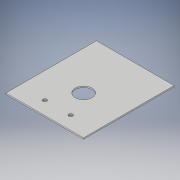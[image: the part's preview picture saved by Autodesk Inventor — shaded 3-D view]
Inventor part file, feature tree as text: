
AUTODESK INVENTOR PART (.ipt)
format: ipt  version: 2019 (Build 230136000, 136)  size: 104,960 bytes
history: native  units: mm
features: extrude x3, sketch x3
ambient origin geometry x8: Origin, YZ Plane, XZ Plane, XY Plane, X Axis, Y Axis, Z Axis, Center Point
bodies: Solid1 (feature_tree)
feature tree (6):
  extrude  "Extrusion1"  Depth=70.0mm
  extrude  "Extrusion2"  Depth=1.0mm
  extrude  "Extrusion3"  Depth=1.0mm TaperAngle=0.0deg
  sketch  "Sketch1"  dims[d0=60.0mm d1=70.0mm]
  sketch  "Sketch2"  dims[d2=1.0mm d3=0.0mm d4=3.0mm]
  sketch  "Sketch3"  dims[d5=3.0mm d6=1.0mm d7=0.0mm d8=13.0mm d9=1.0mm d10=0.0mm]
